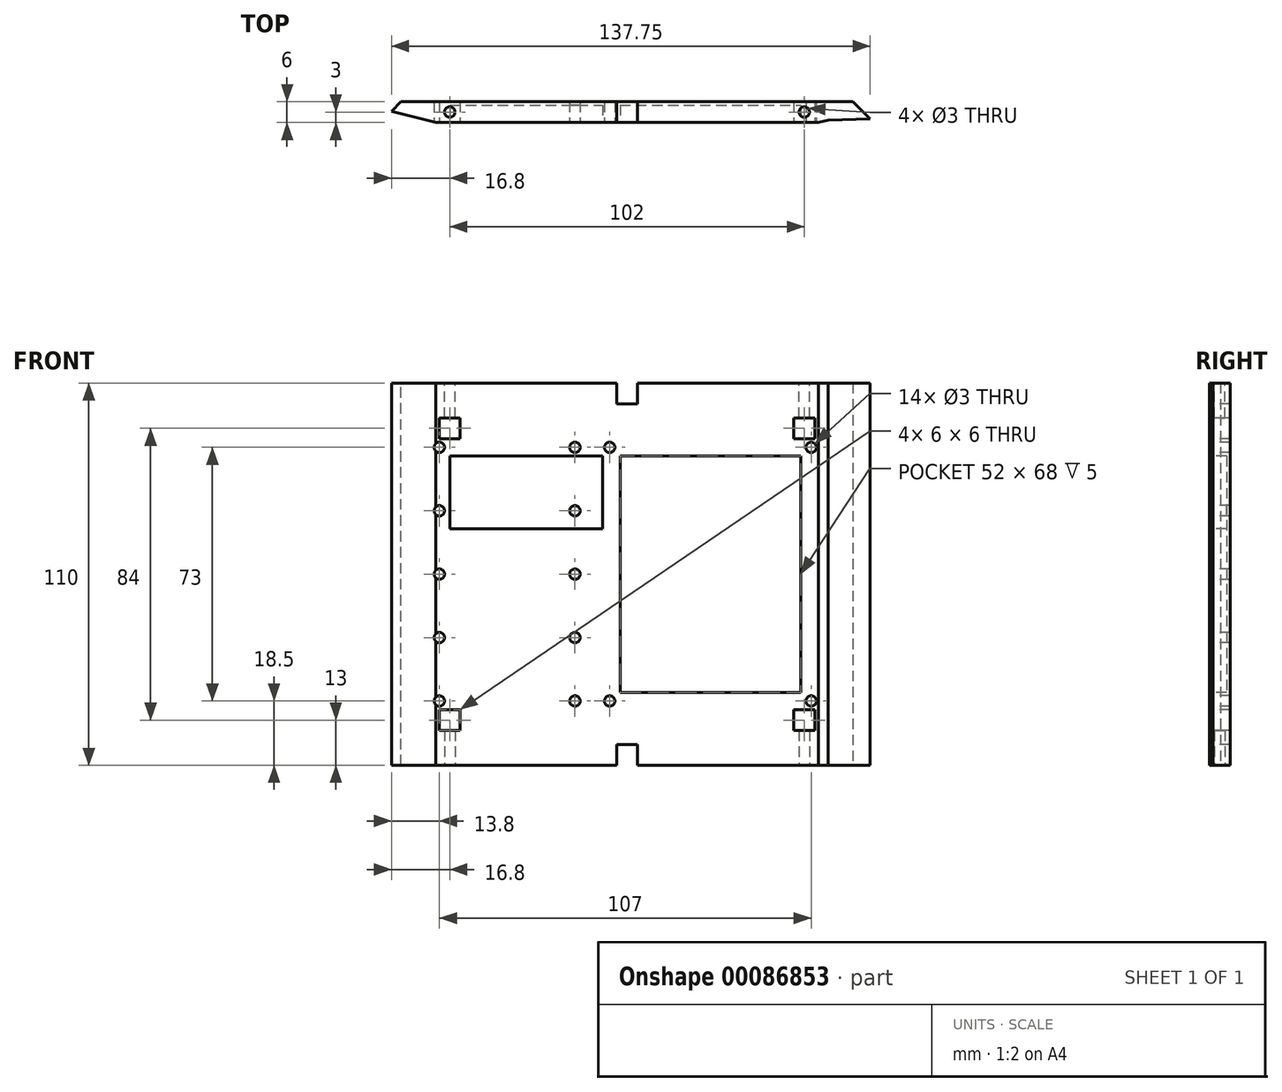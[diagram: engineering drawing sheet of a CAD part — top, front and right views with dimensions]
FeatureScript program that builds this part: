
annotation { "Feature Type Name" : "Feature", "Feature Type Description" : "" }
export const myFeature = defineFeature(function(context is Context, id is Id, definition is map)
    precondition{}
    {
        {
            var Q0;
            Q0=qCreatedBy(makeId("Front.planeOp"),FACE);
            var sketch = newSketch(context, id + "F0", { "sketchPlane" : qUnion([Q0])});
            skLineSegment(sketch, "E0", {"start": v(-51, 0) * mm, "end": v(51, 0) * mm, "construction": true});
            skLineSegment(sketch, "E1.bottom", {"start": v(-70, 55) * mm, "end": v(70, 55) * mm});
            skLineSegment(sketch, "E1.top", {"start": v(-70, -55) * mm, "end": v(70, -55) * mm});
            skLineSegment(sketch, "E1.left", {"start": v(-70, 55) * mm, "end": v(-70, -55) * mm});
            skLineSegment(sketch, "E1.right", {"start": v(70, 55) * mm, "end": v(70, -55) * mm});
            skSolve(sketch);
        }
        {
            var Q0;
            Q0=makeQuery(id+"F0.imprint","IMPRINT",FACE,{"disambiguationData":[TD([[makeQuery(id+"F0.imprint","IMPRINT",EDGE,{"derivedFrom":sQuery(id+"F0.wireOp",EDGE,"E1.bottom")}),-1.0]])]});
            extrude(context, id + "F1", {"entities" : qUnion([Q0]), "depth" : 6 * mm});
        }
        {
            var Q0;
            Q0=makeQuery(id+"F1.opExtrude","SWEPT_FACE",FACE,{"disambiguationData":[OSD([sQuery(id+"F0.wireOp",EDGE,"E1.top")])]});
            var sketch = newSketch(context, id + "F2", { "sketchPlane" : qUnion([Q0])});
            skLineSegment(sketch, "E2", {"start": v(-51, 3) * mm, "end": v(51, 3) * mm, "construction": true});
            skSolve(sketch);
        }
        {
            var Q0;
            Q0=sQuery(id+"F2.wireOp",VERTEX,"E2.start");
            var Q1;
            Q1=sQuery(id+"F2.wireOp",VERTEX,"E2.end");
            var Q2;
            Q2=makeQuery(id+"F1.opExtrude","SWEPT_BODY",BODY,{"disambiguationData":[OSD([sQuery(id+"F0.wireOp",EDGE,"E1.bottom"),sQuery(id+"F0.wireOp",EDGE,"E1.top"),sQuery(id+"F0.wireOp",EDGE,"E1.left"),sQuery(id+"F0.wireOp",EDGE,"E1.right")])]});
            hole(context, id + "F3", {"style" : HoleStyle.SIMPLE, "endStyle" : HoleEndStyle.BLIND, "holeDiameter" : 3 * mm, "holeDepth" : 10 * mm, "locations" : qUnion([Q0, Q1]), "scope" : qUnion([Q2])});
        }
        {
            var Q0;
            Q0=makeQuery(id+"F1.opExtrude","SWEPT_FACE",FACE,{"disambiguationData":[OSD([sQuery(id+"F0.wireOp",EDGE,"E1.bottom")])]});
            var sketch = newSketch(context, id + "F4", { "sketchPlane" : qUnion([Q0])});
            skLineSegment(sketch, "E3", {"start": v(51, -3) * mm, "end": v(-51, -3) * mm, "construction": true});
            skSolve(sketch);
        }
        {
            var Q0;
            Q0=sQuery(id+"F4.wireOp",VERTEX,"E3.start");
            var Q1;
            Q1=sQuery(id+"F4.wireOp",VERTEX,"E3.end");
            var Q2;
            Q2=makeQuery(id+"F1.opExtrude","SWEPT_BODY",BODY,{"disambiguationData":[OSD([sQuery(id+"F0.wireOp",EDGE,"E1.bottom"),sQuery(id+"F0.wireOp",EDGE,"E1.top"),sQuery(id+"F0.wireOp",EDGE,"E1.left"),sQuery(id+"F0.wireOp",EDGE,"E1.right")])]});
            hole(context, id + "F5", {"style" : HoleStyle.SIMPLE, "endStyle" : HoleEndStyle.BLIND, "holeDiameter" : 3 * mm, "holeDepth" : 10 * mm, "locations" : qUnion([Q0, Q1]), "scope" : qUnion([Q2])});
        }
        {
            var Q0;
            Q0=makeQuery(id+"F1.opExtrude","CAP_EDGE",EDGE,{"disambiguationData":[OSD([sQuery(id+"F0.wireOp",EDGE,"E1.left")])],"isStart":true});
            var Q1;
            Q1=makeQuery(id+"F1.opExtrude","CAP_EDGE",EDGE,{"disambiguationData":[OSD([sQuery(id+"F0.wireOp",EDGE,"E1.right")])],"isStart":true});
            chamfer(context, id + "F6", {"entities" : qUnion([Q0, Q1]), "width" : 5 * mm, "tangentPropagation" : true});
        }
        {
            var Q0;
            Q0=makeQuery(id+"F1.opExtrude","CAP_FACE",FACE,{"disambiguationData":[OSD([sQuery(id+"F0.wireOp",EDGE,"E1.bottom"),sQuery(id+"F0.wireOp",EDGE,"E1.top"),sQuery(id+"F0.wireOp",EDGE,"E1.left"),sQuery(id+"F0.wireOp",EDGE,"E1.right")])],"isStart":false});
            var sketch = newSketch(context, id + "F7", { "sketchPlane" : qUnion([Q0])});
            skLineSegment(sketch, "E4.bottom", {"start": v(-54, -39) * mm, "end": v(-48, -39) * mm});
            skLineSegment(sketch, "E4.top", {"start": v(-54, -45) * mm, "end": v(-48, -45) * mm});
            skLineSegment(sketch, "E4.left", {"start": v(-54, -39) * mm, "end": v(-54, -45) * mm});
            skLineSegment(sketch, "E4.right", {"start": v(-48, -39) * mm, "end": v(-48, -45) * mm});
            skLineSegment(sketch, "E5.bottom", {"start": v(48, -39) * mm, "end": v(54, -39) * mm});
            skLineSegment(sketch, "E5.top", {"start": v(48, -45) * mm, "end": v(54, -45) * mm});
            skLineSegment(sketch, "E5.left", {"start": v(48, -39) * mm, "end": v(48, -45) * mm});
            skLineSegment(sketch, "E5.right", {"start": v(54, -39) * mm, "end": v(54, -45) * mm});
            skLineSegment(sketch, "E6.bottom", {"start": v(48, 45) * mm, "end": v(54, 45) * mm});
            skLineSegment(sketch, "E6.top", {"start": v(48, 39) * mm, "end": v(54, 39) * mm});
            skLineSegment(sketch, "E6.left", {"start": v(48, 45) * mm, "end": v(48, 39) * mm});
            skLineSegment(sketch, "E6.right", {"start": v(54, 45) * mm, "end": v(54, 39) * mm});
            skLineSegment(sketch, "E7.bottom", {"start": v(-54, 45) * mm, "end": v(-48, 45) * mm});
            skLineSegment(sketch, "E7.top", {"start": v(-54, 39) * mm, "end": v(-48, 39) * mm});
            skLineSegment(sketch, "E7.left", {"start": v(-54, 45) * mm, "end": v(-54, 39) * mm});
            skLineSegment(sketch, "E7.right", {"start": v(-48, 45) * mm, "end": v(-48, 39) * mm});
            skLineSegment(sketch, "E8", {"start": v(0, -55) * mm, "end": v(0, 55) * mm, "construction": true});
            skLineSegment(sketch, "E9.bottom", {"start": v(-3, -55) * mm, "end": v(3, -55) * mm});
            skLineSegment(sketch, "E9.top", {"start": v(-3, -49) * mm, "end": v(3, -49) * mm});
            skLineSegment(sketch, "E9.left", {"start": v(-3, -55) * mm, "end": v(-3, -49) * mm});
            skLineSegment(sketch, "E9.right", {"start": v(3, -55) * mm, "end": v(3, -49) * mm});
            skLineSegment(sketch, "E10.bottom", {"start": v(3, 55) * mm, "end": v(-3, 55) * mm});
            skLineSegment(sketch, "E10.top", {"start": v(3, 49) * mm, "end": v(-3, 49) * mm});
            skLineSegment(sketch, "E10.left", {"start": v(3, 55) * mm, "end": v(3, 49) * mm});
            skLineSegment(sketch, "E10.right", {"start": v(-3, 55) * mm, "end": v(-3, 49) * mm});
            skSolve(sketch);
        }
        {
            var Q0;
            Q0 = qSketchRegion(id + "F7", true);
            extrude(context, id + "F8", {"entities" : qUnion([Q0]), "operationType" : NewBodyOperationType.REMOVE, "endBound" : BoundingType.THROUGH_ALL, "oppositeDirection" : true, "depth" : 25 * mm});
        }
        {
            var Q0;
            Q0=makeQuery(id+"F1.opExtrude","CAP_FACE",FACE,{"disambiguationData":[OSD([sQuery(id+"F0.wireOp",EDGE,"E1.bottom"),sQuery(id+"F0.wireOp",EDGE,"E1.top"),sQuery(id+"F0.wireOp",EDGE,"E1.left"),sQuery(id+"F0.wireOp",EDGE,"E1.right")])],"isStart":false});
            var sketch = newSketch(context, id + "F9", { "sketchPlane" : qUnion([Q0])});
            skLineSegment(sketch, "E11.bottom", {"start": v(-2, 34) * mm, "end": v(50, 34) * mm});
            skLineSegment(sketch, "E11.top", {"start": v(-2, -34) * mm, "end": v(50, -34) * mm});
            skLineSegment(sketch, "E11.left", {"start": v(-2, 34) * mm, "end": v(-2, -34) * mm});
            skLineSegment(sketch, "E11.right", {"start": v(50, 34) * mm, "end": v(50, -34) * mm});
            skLineSegment(sketch, "E12", {"start": v(-70, 0) * mm, "end": v(70, 0) * mm, "construction": true});
            skLineSegment(sketch, "E13.bottom", {"start": v(-51, 34) * mm, "end": v(-7, 34) * mm});
            skLineSegment(sketch, "E13.top", {"start": v(-51, 13) * mm, "end": v(-7, 13) * mm});
            skLineSegment(sketch, "E13.left", {"start": v(-51, 34) * mm, "end": v(-51, 13) * mm});
            skLineSegment(sketch, "E13.right", {"start": v(-7, 34) * mm, "end": v(-7, 13) * mm});
            skSolve(sketch);
        }
        {
            var Q0;
            Q0=makeQuery(id+"F9.imprint","IMPRINT",FACE,{"disambiguationData":[TD([[makeQuery(id+"F9.imprint","IMPRINT",EDGE,{"derivedFrom":sQuery(id+"F9.wireOp",EDGE,"E11.bottom")}),-1.0]])]});
            var Q1;
            Q1=makeQuery(id+"F9.imprint","IMPRINT",FACE,{"disambiguationData":[TD([[makeQuery(id+"F9.imprint","IMPRINT",EDGE,{"derivedFrom":sQuery(id+"F9.wireOp",EDGE,"E13.bottom")}),-1.0]])]});
            extrude(context, id + "F10", {"entities" : qUnion([Q0, Q1]), "operationType" : NewBodyOperationType.REMOVE, "oppositeDirection" : true, "depth" : 5 * mm});
        }
        {
            var Q0;
            Q0=makeQuery(id+"F1.opExtrude","CAP_FACE",FACE,{"disambiguationData":[OSD([sQuery(id+"F0.wireOp",EDGE,"E1.bottom"),sQuery(id+"F0.wireOp",EDGE,"E1.top"),sQuery(id+"F0.wireOp",EDGE,"E1.left"),sQuery(id+"F0.wireOp",EDGE,"E1.right")])],"isStart":false});
            var sketch = newSketch(context, id + "F11", { "sketchPlane" : qUnion([Q0])});
            skCircle(sketch, "E14", {"center": v(-54, 36.5) * mm, "radius": 1.5 * mm});
            skCircle(sketch, "E15", {"center": v(-5, 36.5) * mm, "radius": 1.5 * mm});
            skCircle(sketch, "E16", {"center": v(-15, 36.5) * mm, "radius": 1.5 * mm});
            skCircle(sketch, "E17", {"center": v(53, 36.5) * mm, "radius": 1.5 * mm});
            skLineSegment(sketch, "E18", {"start": v(-70, 0) * mm, "end": v(70, 0) * mm, "construction": true});
            skCircle(sketch, "E19", {"center": v(-54, 18.25) * mm, "radius": 1.5 * mm});
            skCircle(sketch, "E20", {"center": v(-15, 18.25) * mm, "radius": 1.5 * mm});
            skCircle(sketch, "E21", {"center": v(-54, 0) * mm, "radius": 1.5 * mm});
            skCircle(sketch, "E22", {"center": v(-15, 0) * mm, "radius": 1.5 * mm});
            skCircle(sketch, "E23.MirrorC", {"center": v(-54, -36.5) * mm, "radius": 1.5 * mm});
            skCircle(sketch, "E24.MirrorC", {"center": v(-5, -36.5) * mm, "radius": 1.5 * mm});
            skCircle(sketch, "E25.MirrorC", {"center": v(-15, -36.5) * mm, "radius": 1.5 * mm});
            skCircle(sketch, "E26.MirrorC", {"center": v(53, -36.5) * mm, "radius": 1.5 * mm});
            skCircle(sketch, "E27.MirrorC", {"center": v(-54, -18.25) * mm, "radius": 1.5 * mm});
            skCircle(sketch, "E28.MirrorC", {"center": v(-15, -18.25) * mm, "radius": 1.5 * mm});
            skSolve(sketch);
        }
        {
            var Q0;
            Q0 = qSketchRegion(id + "F11", true);
            extrude(context, id + "F12", {"entities" : qUnion([Q0]), "operationType" : NewBodyOperationType.REMOVE, "oppositeDirection" : true, "depth" : 25 * mm});
        }
        {
            var Q0;
            {var subQ0=sQuery(id+"F0.wireOp",EDGE,"E1.right");var subQ2=sQuery(id+"F0.wireOp",EDGE,"E1.top");Q0=makeQuery(id+"F8.boolean.opBoolean","SPLIT",FACE,{"disambiguationData":[TD([makeQuery(id+"F1.opExtrude","SWEPT_FACE",FACE,{"disambiguationData":[OSD([subQ0])]})])],"derivedFrom":makeQuery(id+"F1.opExtrude","SWEPT_FACE",FACE,{"disambiguationData":[OSD([subQ2])]})});}
            var sketch = newSketch(context, id + "F13", { "sketchPlane" : qUnion([Q0])});
            skLineSegment(sketch, "E29", {"start": v(55.06, 6) * mm, "end": v(57.86, 5.3) * mm});
            skLineSegment(sketch, "E30", {"start": v(57.86, 5.3) * mm, "end": v(69.95, 4.95) * mm});
            skSolve(sketch);
        }
        {
            var Q0;
            {var subQ6=sQuery(id+"F13.wireOp",EDGE,"E29");Q0=makeQuery(id+"F13.imprint","IMPRINT",FACE,{"disambiguationData":[TD([[makeQuery(id+"F13.imprint","IMPRINT",EDGE,{"derivedFrom":subQ6}),1.0]])]});}
            extrude(context, id + "F14", {"entities" : qUnion([Q0]), "operationType" : NewBodyOperationType.REMOVE, "endBound" : BoundingType.THROUGH_ALL, "oppositeDirection" : true, "depth" : 25 * mm});
        }
        {
            var Q0;
            {var subQ0=sQuery(id+"F0.wireOp",EDGE,"E1.left");var subQ2=sQuery(id+"F0.wireOp",EDGE,"E1.top");Q0=makeQuery(id+"F8.boolean.opBoolean","SPLIT",FACE,{"disambiguationData":[TD([makeQuery(id+"F1.opExtrude","SWEPT_FACE",FACE,{"disambiguationData":[OSD([subQ0])]})])],"derivedFrom":makeQuery(id+"F1.opExtrude","SWEPT_FACE",FACE,{"disambiguationData":[OSD([subQ2])]})});}
            var sketch = newSketch(context, id + "F15", { "sketchPlane" : qUnion([Q0])});
            skLineSegment(sketch, "E31", {"start": v(-67.8, 2.8) * mm, "end": v(-55, 6) * mm});
            skSolve(sketch);
        }
        {
            var Q0;
            {var subQ0=sQuery(id+"F15.wireOp",EDGE,"E31");Q0=makeQuery(id+"F15.imprint","IMPRINT",FACE,{"disambiguationData":[TD([[makeQuery(id+"F15.imprint","IMPRINT",EDGE,{"derivedFrom":subQ0}),1.0]])]});}
            extrude(context, id + "F16", {"entities" : qUnion([Q0]), "operationType" : NewBodyOperationType.REMOVE, "endBound" : BoundingType.THROUGH_ALL, "oppositeDirection" : true, "depth" : 25 * mm});
        }
    });
